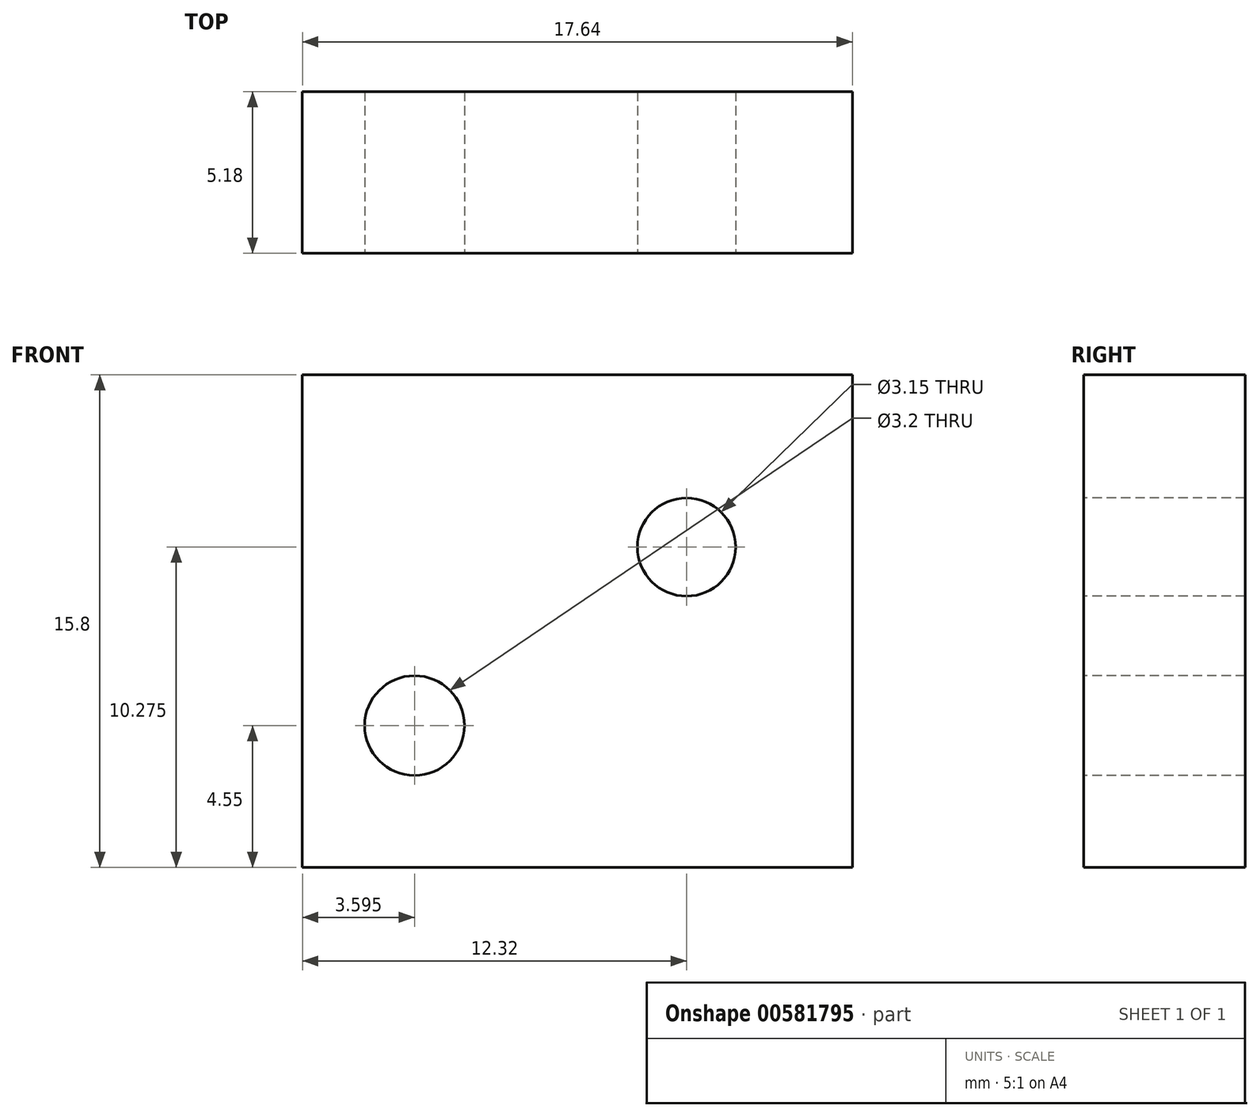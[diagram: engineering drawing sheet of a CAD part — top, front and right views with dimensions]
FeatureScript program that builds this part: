
annotation { "Feature Type Name" : "Feature", "Feature Type Description" : "" }
export const myFeature = defineFeature(function(context is Context, id is Id, definition is map)
    precondition{}
    {
        {
            var Q0;
            Q0=qCreatedBy(makeId("Front.planeOp"),FACE);
            var sketch = newSketch(context, id + "F0", { "sketchPlane" : qUnion([Q0])});
            skLineSegment(sketch, "E0.bottom", {"start": v(-8.82, 7.9) * mm, "end": v(8.82, 7.9) * mm});
            skLineSegment(sketch, "E0.top", {"start": v(-8.82, -7.9) * mm, "end": v(8.82, -7.9) * mm});
            skLineSegment(sketch, "E0.left", {"start": v(-8.82, 7.9) * mm, "end": v(-8.82, -7.9) * mm});
            skLineSegment(sketch, "E0.right", {"start": v(8.82, 7.9) * mm, "end": v(8.82, -7.9) * mm});
            skPoint(sketch, "E0.middle", {"position": v(0, 0) * mm});
            skSolve(sketch);
        }
        {
            var Q0;
            Q0 = qSketchRegion(id + "F0", true);
            extrude(context, id + "F1", {"entities" : qUnion([Q0]), "depth" : 5.18 * mm, "offsetDistance" : 25 * mm});
        }
        {
            var Q0;
            Q0=makeQuery(id+"F1.opExtrude","CAP_FACE",FACE,{"disambiguationData":[OSD([sQuery(id+"F0.wireOp",EDGE,"E0.bottom"),sQuery(id+"F0.wireOp",EDGE,"E0.top"),sQuery(id+"F0.wireOp",EDGE,"E0.left"),sQuery(id+"F0.wireOp",EDGE,"E0.right")])],"isStart":false});
            var sketch = newSketch(context, id + "F2", { "sketchPlane" : qUnion([Q0])});
            skCircle(sketch, "E1", {"center": v(3.5, 2.37) * mm, "radius": 1.57 * mm});
            skCircle(sketch, "E2", {"center": v(-5.22, -3.35) * mm, "radius": 1.6 * mm});
            skSolve(sketch);
        }
        {
            var Q0;
            Q0=makeQuery(id+"F2.imprint","IMPRINT",FACE,{"disambiguationData":[TD([[makeQuery(id+"F2.imprint","IMPRINT",EDGE,{"derivedFrom":sQuery(id+"F2.wireOp",EDGE,"E2")}),1.0]])]});
            var Q1;
            Q1=makeQuery(id+"F2.imprint","IMPRINT",FACE,{"disambiguationData":[TD([[makeQuery(id+"F2.imprint","IMPRINT",EDGE,{"derivedFrom":sQuery(id+"F2.wireOp",EDGE,"E1")}),1.0]])]});
            extrude(context, id + "F3", {"entities" : qUnion([Q0, Q1]), "operationType" : NewBodyOperationType.REMOVE, "endBound" : BoundingType.THROUGH_ALL, "oppositeDirection" : true, "depth" : 25 * mm, "offsetDistance" : 25 * mm});
        }
    });
